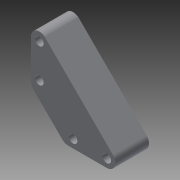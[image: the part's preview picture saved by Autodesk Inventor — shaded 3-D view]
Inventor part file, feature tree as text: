
AUTODESK INVENTOR PART (.ipt)
format: ipt  version: 2014 (Build 180170000, 170)  size: 95,744 bytes
history: native  units: in
note: dims shown in document units (in); Inventor stores cm internally (conversion verified against a paired STEP export)
features: extrude x1, sketch x1
ambient origin geometry x8: Origin, YZ Plane, XZ Plane, XY Plane, X Axis, Y Axis, Z Axis, Center Point
bodies: Solid1 (feature_tree)
feature tree (2):
  extrude  "Extrusion1"  Depth=0.25in
  sketch  "Sketch1"  dims[d6=0.25in d7=0.25in d8=0.25in d9=0.25in d10=0.25in d11=1.0in d12=0.0in]
